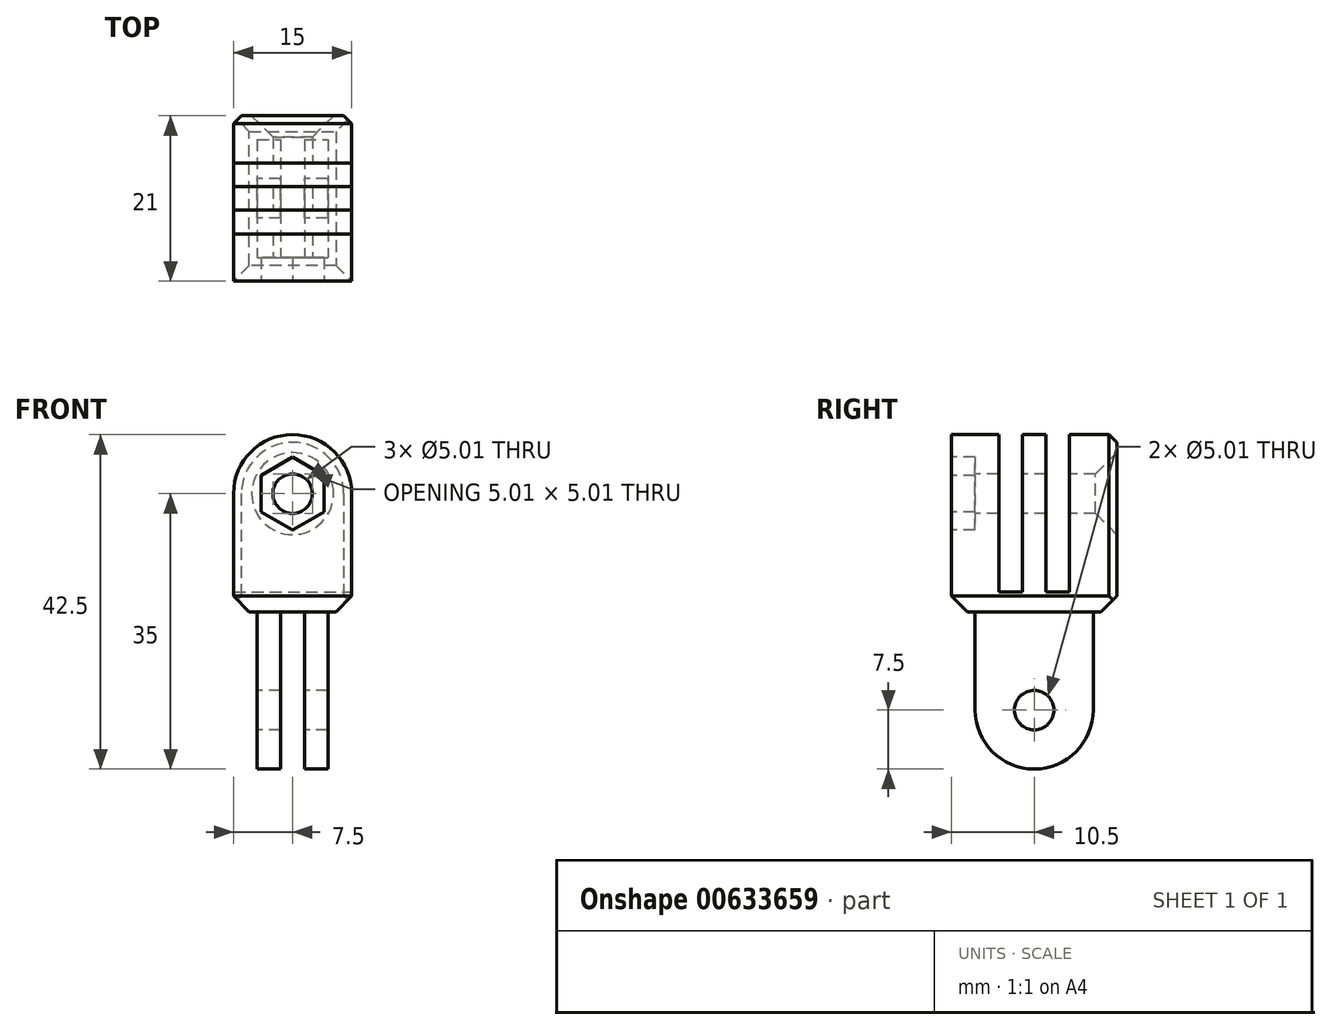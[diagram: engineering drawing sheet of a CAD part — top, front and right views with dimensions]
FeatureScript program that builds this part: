
annotation { "Feature Type Name" : "Feature", "Feature Type Description" : "" }
export const myFeature = defineFeature(function(context is Context, id is Id, definition is map)
    precondition{}
    {
        {
            var Q0;
            Q0=qCreatedBy(makeId("Top.planeOp"),FACE);
            var sketch = newSketch(context, id + "F0", { "sketchPlane" : qUnion([Q0])});
            skLineSegment(sketch, "E0.bottom", {"start": v(7.5, 10.5) * mm, "end": v(-7.5, 10.5) * mm});
            skLineSegment(sketch, "E0.top", {"start": v(7.5, -10.5) * mm, "end": v(-7.5, -10.5) * mm});
            skLineSegment(sketch, "E0.left", {"start": v(7.5, 10.5) * mm, "end": v(7.5, -10.5) * mm});
            skLineSegment(sketch, "E0.right", {"start": v(-7.5, 10.5) * mm, "end": v(-7.5, -10.5) * mm});
            skPoint(sketch, "E0.middle", {"position": v(0, 0) * mm});
            skSolve(sketch);
        }
        {
            var Q0;
            Q0 = qSketchRegion(id + "F0", true);
            extrude(context, id + "F1", {"entities" : qUnion([Q0]), "depth" : 2.5 * mm, "offsetDistance" : 25 * mm, "symmetric" : true});
        }
        {
            var Q0;
            Q0=makeQuery(id+"F1.opExtrude","CAP_FACE",FACE,{"disambiguationData":[OSD([sQuery(id+"F0.wireOp",EDGE,"E0.bottom"),sQuery(id+"F0.wireOp",EDGE,"E0.top"),sQuery(id+"F0.wireOp",EDGE,"E0.left"),sQuery(id+"F0.wireOp",EDGE,"E0.right")])],"isStart":false});
            var sketch = newSketch(context, id + "F2", { "sketchPlane" : qUnion([Q0])});
            skLineSegment(sketch, "E1", {"start": v(-7.5, 10.5) * mm, "end": v(-7.5, 4.5) * mm, "construction": true});
            skLineSegment(sketch, "E2", {"start": v(-7.5, 4.5) * mm, "end": v(-7.5, 1.5) * mm, "construction": true});
            skLineSegment(sketch, "E3", {"start": v(-7.5, 1.5) * mm, "end": v(-7.5, -1.5) * mm, "construction": true});
            skLineSegment(sketch, "E4", {"start": v(-7.5, -1.5) * mm, "end": v(-7.5, -4.5) * mm, "construction": true});
            skLineSegment(sketch, "E5", {"start": v(-7.5, 4.5) * mm, "end": v(7.5, 4.5) * mm});
            skLineSegment(sketch, "E6", {"start": v(-7.5, 1.5) * mm, "end": v(7.5, 1.5) * mm});
            skLineSegment(sketch, "E7", {"start": v(-7.5, -1.5) * mm, "end": v(7.5, -1.5) * mm});
            skLineSegment(sketch, "E8", {"start": v(-7.5, -4.5) * mm, "end": v(7.5, -4.5) * mm});
            skSolve(sketch);
        }
        {
            var Q0;
            Q0 = qSketchRegion(id + "F2", true);
            var Q1;
            {var subQ0=sQuery(id+"F2.wireOp",EDGE,"E8");Q1=makeQuery(id+"F2.imprint","IMPRINT",FACE,{"disambiguationData":[TD([[makeQuery(id+"F2.imprint","IMPRINT",EDGE,{"derivedFrom":subQ0}),-1.0]])]});}
            var Q2;
            {var subQ0=sQuery(id+"F2.wireOp",EDGE,"E6");Q2=makeQuery(id+"F2.imprint","IMPRINT",FACE,{"disambiguationData":[TD([[makeQuery(id+"F2.imprint","IMPRINT",EDGE,{"derivedFrom":subQ0}),-1.0]])]});}
            var Q3;
            {var subQ0=sQuery(id+"F2.wireOp",EDGE,"E5");Q3=makeQuery(id+"F2.imprint","IMPRINT",FACE,{"disambiguationData":[TD([[makeQuery(id+"F2.imprint","IMPRINT",EDGE,{"derivedFrom":subQ0}),1.0]])]});}
            extrude(context, id + "F3", {"entities" : qUnion([Q0, Q1, Q2, Q3]), "operationType" : NewBodyOperationType.ADD, "depth" : 20 * mm, "offsetDistance" : 25 * mm});
        }
        {
            var Q0;
            Q0=makeQuery(id+"F1.opExtrude","CAP_FACE",FACE,{"disambiguationData":[OSD([sQuery(id+"F0.wireOp",EDGE,"E0.bottom"),sQuery(id+"F0.wireOp",EDGE,"E0.top"),sQuery(id+"F0.wireOp",EDGE,"E0.left"),sQuery(id+"F0.wireOp",EDGE,"E0.right")])],"isStart":true});
            var sketch = newSketch(context, id + "F4", { "sketchPlane" : qUnion([Q0])});
            skLineSegment(sketch, "E9", {"start": v(-7.5, -10.5) * mm, "end": v(-4.5, -10.5) * mm, "construction": true});
            skLineSegment(sketch, "E10", {"start": v(-4.5, -10.5) * mm, "end": v(-1.5, -10.5) * mm, "construction": true});
            skLineSegment(sketch, "E11", {"start": v(-1.5, -10.5) * mm, "end": v(1.5, -10.5) * mm, "construction": true});
            skLineSegment(sketch, "E12", {"start": v(1.5, -10.5) * mm, "end": v(4.5, -10.5) * mm, "construction": true});
            skLineSegment(sketch, "E13", {"start": v(-4.5, -10.5) * mm, "end": v(-4.5, -7.5) * mm, "construction": true});
            skLineSegment(sketch, "E14", {"start": v(-7.5, 10.5) * mm, "end": v(-4.5, 10.5) * mm, "construction": true});
            skLineSegment(sketch, "E15", {"start": v(-4.5, 10.5) * mm, "end": v(-1.5, 10.5) * mm, "construction": true});
            skLineSegment(sketch, "E16", {"start": v(-1.5, 10.5) * mm, "end": v(1.5, 10.5) * mm, "construction": true});
            skLineSegment(sketch, "E17", {"start": v(1.5, 10.5) * mm, "end": v(4.5, 10.5) * mm, "construction": true});
            skLineSegment(sketch, "E18", {"start": v(4.5, 10.5) * mm, "end": v(4.5, 7.5) * mm, "construction": true});
            skLineSegment(sketch, "E19", {"start": v(4.5, 7.5) * mm, "end": v(1.5, 7.5) * mm, "construction": true});
            skLineSegment(sketch, "E20", {"start": v(1.5, 7.5) * mm, "end": v(-1.5, 7.5) * mm, "construction": true});
            skLineSegment(sketch, "E21", {"start": v(1.5, -10.5) * mm, "end": v(1.5, -7.5) * mm, "construction": true});
            skLineSegment(sketch, "E22.bottom", {"start": v(-4.5, -7.5) * mm, "end": v(-1.5, -7.5) * mm});
            skLineSegment(sketch, "E22.top", {"start": v(-4.5, 7.5) * mm, "end": v(-1.5, 7.5) * mm});
            skLineSegment(sketch, "E22.left", {"start": v(-4.5, -7.5) * mm, "end": v(-4.5, 7.5) * mm});
            skLineSegment(sketch, "E22.right", {"start": v(-1.5, -7.5) * mm, "end": v(-1.5, 7.5) * mm});
            skLineSegment(sketch, "E23.bottom", {"start": v(1.5, -7.5) * mm, "end": v(4.5, -7.5) * mm});
            skLineSegment(sketch, "E23.top", {"start": v(1.5, 7.5) * mm, "end": v(4.5, 7.5) * mm});
            skLineSegment(sketch, "E23.left", {"start": v(1.5, -7.5) * mm, "end": v(1.5, 7.5) * mm});
            skLineSegment(sketch, "E23.right", {"start": v(4.5, -7.5) * mm, "end": v(4.5, 7.5) * mm});
            skSolve(sketch);
        }
        {
            var Q0;
            Q0=makeQuery(id+"F4.imprint","IMPRINT",FACE,{"disambiguationData":[TD([[makeQuery(id+"F4.imprint","IMPRINT",EDGE,{"derivedFrom":sQuery(id+"F4.wireOp",EDGE,"E22.bottom")}),1.0]])]});
            var Q1;
            Q1=makeQuery(id+"F4.imprint","IMPRINT",FACE,{"disambiguationData":[TD([[makeQuery(id+"F4.imprint","IMPRINT",EDGE,{"derivedFrom":sQuery(id+"F4.wireOp",EDGE,"E23.bottom")}),1.0]])]});
            extrude(context, id + "F5", {"entities" : qUnion([Q0, Q1]), "operationType" : NewBodyOperationType.ADD, "depth" : 20 * mm, "offsetDistance" : 25 * mm});
        }
        {
            var Q0;
            {var subQ0=sQuery(id+"F0.wireOp",EDGE,"E0.top");Q0=makeQuery(id+"F3.boolean.opBoolean","MERGE",FACE,{"derivedFrom":[makeQuery(id+"F1.opExtrude","SWEPT_FACE",FACE,{"disambiguationData":[OSD([subQ0])]}),makeQuery(id+"F3.opExtrude","SWEPT_FACE",FACE,{"disambiguationData":[OSD([subQ0])]})]});}
            var sketch = newSketch(context, id + "F6", { "sketchPlane" : qUnion([Q0])});
            skLineSegment(sketch, "E24", {"start": v(0, 21.25) * mm, "end": v(0, 13.75) * mm, "construction": true});
            skPoint(sketch, "E24.endSnap0", {"position": v(0, 21.25) * mm});
            skCircle(sketch, "E25", {"center": v(0, 13.75) * mm, "radius": 7.5 * mm});
            skCircle(sketch, "E26", {"center": v(0, 13.75) * mm, "radius": 2.5 * mm});
            skCircle(sketch, "E27.cCircle", {"center": v(0, 13.75) * mm, "radius": 4.01 * mm, "construction": true});
            skLineSegment(sketch, "E27.0", {"start": v(0, 18.38) * mm, "end": v(4, 16.07) * mm});
            skLineSegment(sketch, "E27.1", {"start": v(4, 16.07) * mm, "end": v(4.01, 11.44) * mm});
            skLineSegment(sketch, "E27.2", {"start": v(4.01, 11.44) * mm, "end": v(0, 9.12) * mm});
            skLineSegment(sketch, "E27.3", {"start": v(0, 9.12) * mm, "end": v(-4, 11.43) * mm});
            skLineSegment(sketch, "E27.4", {"start": v(-4, 11.43) * mm, "end": v(-4.01, 16.06) * mm});
            skLineSegment(sketch, "E27.5", {"start": v(-4.01, 16.06) * mm, "end": v(0, 18.38) * mm});
            skPoint(sketch, "E27.0.midPoint", {"position": v(2, 17.22) * mm});
            skLineSegment(sketch, "E28", {"start": v(0, 13.75) * mm, "end": v(2, 17.22) * mm, "construction": true});
            skSolve(sketch);
        }
        {
            var Q0;
            {var subQ0=sQuery(id+"F6.wireOp",EDGE,"E25");var subQ1=sQuery(id+"F0.wireOp",EDGE,"E0.top");var subQ2=makeQuery(id+"F3.opExtrude","CAP_EDGE",EDGE,{"disambiguationData":[OSD([subQ1])],"isStart":false});var subQ3=makeQuery(id+"F6.imprint","INTERSECT",VERTEX,{"derivedFrom":[subQ2,subQ0]});Q0=makeQuery(id+"F6.imprint","IMPRINT",FACE,{"disambiguationData":[TD([[makeQuery(id+"F6.imprint","IMPRINT",EDGE,{"disambiguationData":[TD([[subQ3,1.0]])],"derivedFrom":subQ0}),-1.0]])]});}
            var Q1;
            {var subQ0=sQuery(id+"F6.wireOp",EDGE,"E25");var subQ1=sQuery(id+"F0.wireOp",EDGE,"E0.top");var subQ2=makeQuery(id+"F3.opExtrude","CAP_EDGE",EDGE,{"disambiguationData":[OSD([subQ1])],"isStart":false});var subQ3=makeQuery(id+"F6.imprint","INTERSECT",VERTEX,{"derivedFrom":[subQ2,subQ0]});Q1=makeQuery(id+"F6.imprint","IMPRINT",FACE,{"disambiguationData":[TD([[makeQuery(id+"F6.imprint","IMPRINT",EDGE,{"disambiguationData":[TD([[subQ3,-1.0]])],"derivedFrom":subQ0}),-1.0]])]});}
            var Q2;
            Q2=makeQuery(id+"F6.imprint","IMPRINT",FACE,{"disambiguationData":[TD([[makeQuery(id+"F6.imprint","IMPRINT",EDGE,{"derivedFrom":sQuery(id+"F6.wireOp",EDGE,"E26")}),1.0]])]});
            extrude(context, id + "F7", {"entities" : qUnion([Q0, Q1, Q2]), "operationType" : NewBodyOperationType.REMOVE, "oppositeDirection" : true, "depth" : 25 * mm, "offsetDistance" : 25 * mm});
        }
        {
            var Q0;
            Q0=makeQuery(id+"F5.opExtrude","SWEPT_FACE",FACE,{"disambiguationData":[OSD([sQuery(id+"F4.wireOp",EDGE,"E22.left")])]});
            var sketch = newSketch(context, id + "F8", { "sketchPlane" : qUnion([Q0])});
            skLineSegment(sketch, "E29", {"start": v(0, -21.25) * mm, "end": v(0, -13.75) * mm, "construction": true});
            skPoint(sketch, "E29.endSnap0", {"position": v(0, -21.25) * mm});
            skCircle(sketch, "E30", {"center": v(0, -13.75) * mm, "radius": 7.5 * mm});
            skCircle(sketch, "E31", {"center": v(0, -13.75) * mm, "radius": 2.5 * mm});
            skSolve(sketch);
        }
        {
            var Q0;
            {var subQ0=sQuery(id+"F8.wireOp",EDGE,"E30");var subQ1=sQuery(id+"F4.wireOp",EDGE,"E22.left");var subQ4=makeQuery(id+"F5.opExtrude","CAP_EDGE",EDGE,{"disambiguationData":[OSD([subQ1])],"isStart":false});var subQ5=makeQuery(id+"F8.imprint","INTERSECT",VERTEX,{"derivedFrom":[subQ4,subQ0]});Q0=makeQuery(id+"F8.imprint","IMPRINT",FACE,{"disambiguationData":[TD([[makeQuery(id+"F8.imprint","IMPRINT",EDGE,{"disambiguationData":[TD([[subQ5,-1.0]])],"derivedFrom":subQ0}),-1.0]])]});}
            var Q1;
            {var subQ0=sQuery(id+"F8.wireOp",EDGE,"E30");var subQ1=sQuery(id+"F4.wireOp",EDGE,"E22.left");var subQ4=makeQuery(id+"F5.opExtrude","CAP_EDGE",EDGE,{"disambiguationData":[OSD([subQ1])],"isStart":false});var subQ5=makeQuery(id+"F8.imprint","INTERSECT",VERTEX,{"derivedFrom":[subQ4,subQ0]});Q1=makeQuery(id+"F8.imprint","IMPRINT",FACE,{"disambiguationData":[TD([[makeQuery(id+"F8.imprint","IMPRINT",EDGE,{"disambiguationData":[TD([[subQ5,1.0]])],"derivedFrom":subQ0}),-1.0]])]});}
            var Q2;
            Q2=makeQuery(id+"F8.imprint","IMPRINT",FACE,{"disambiguationData":[TD([[makeQuery(id+"F8.imprint","IMPRINT",EDGE,{"derivedFrom":sQuery(id+"F8.wireOp",EDGE,"E31")}),1.0]])]});
            extrude(context, id + "F9", {"entities" : qUnion([Q0, Q1, Q2]), "operationType" : NewBodyOperationType.REMOVE, "oppositeDirection" : true, "depth" : 25 * mm, "offsetDistance" : 25 * mm});
        }
        {
            var Q0;
            Q0=makeQuery(id+"F1.opExtrude","CAP_EDGE",EDGE,{"disambiguationData":[OSD([sQuery(id+"F0.wireOp",EDGE,"E0.right")])],"isStart":true});
            var Q1;
            Q1=makeQuery(id+"F1.opExtrude","CAP_EDGE",EDGE,{"disambiguationData":[OSD([sQuery(id+"F0.wireOp",EDGE,"E0.bottom")])],"isStart":true});
            var Q2;
            Q2=makeQuery(id+"F1.opExtrude","CAP_EDGE",EDGE,{"disambiguationData":[OSD([sQuery(id+"F0.wireOp",EDGE,"E0.top")])],"isStart":true});
            var Q3;
            Q3=makeQuery(id+"F1.opExtrude","CAP_EDGE",EDGE,{"disambiguationData":[OSD([sQuery(id+"F0.wireOp",EDGE,"E0.left")])],"isStart":true});
            chamfer(context, id + "F10", {"entities" : qUnion([Q0, Q1, Q2, Q3]), "width" : 2 * mm, "tangentPropagation" : true});
        }
        {
            var Q0;
            Q0=makeQuery(id+"F6.imprint","IMPRINT",FACE,{"disambiguationData":[TD([[makeQuery(id+"F6.imprint","IMPRINT",EDGE,{"derivedFrom":sQuery(id+"F6.wireOp",EDGE,"E26")}),-1.0]])]});
            extrude(context, id + "F11", {"entities" : qUnion([Q0]), "operationType" : NewBodyOperationType.REMOVE, "oppositeDirection" : true, "depth" : 3 * mm, "offsetDistance" : 25 * mm});
        }
        {
            var Q0;
            {var subQ0=sQuery(id+"F0.wireOp",EDGE,"E0.bottom");Q0=makeQuery(id+"F7.boolean.opBoolean","INTERSECT",EDGE,{"derivedFrom":[makeQuery(id+"F3.boolean.opBoolean","MERGE",FACE,{"derivedFrom":[makeQuery(id+"F1.opExtrude","SWEPT_FACE",FACE,{"disambiguationData":[OSD([subQ0])]}),makeQuery(id+"F3.opExtrude","SWEPT_FACE",FACE,{"disambiguationData":[OSD([subQ0])]})]}),makeQuery(id+"F7.opExtrude","SWEPT_FACE",FACE,{"disambiguationData":[OSD([sQuery(id+"F6.wireOp",EDGE,"E26")])]})]});}
            chamfer(context, id + "F12", {"entities" : qUnion([Q0]), "width" : 2.7 * mm, "tangentPropagation" : true});
        }
        {
            var Q0;
            {var subQ0=sQuery(id+"F6.wireOp",EDGE,"E25");var subQ1=sQuery(id+"F0.wireOp",EDGE,"E0.top");var subQ2=makeQuery(id+"F6.imprint","INTERSECT",VERTEX,{"derivedFrom":[makeQuery(id+"F3.opExtrude","CAP_EDGE",EDGE,{"disambiguationData":[OSD([subQ1])],"isStart":false}),subQ0]});Q0=makeQuery(id+"F7.boolean.opBoolean","TWEAK_EDGE",EDGE,{"derivedFrom":[makeQuery(id+"F7.opExtrude","CAP_EDGE",EDGE,{"disambiguationData":[OSD([subQ0]),TDD([makeQuery(id+"F6.imprint","IMPRINT",EDGE,{"disambiguationData":[TD([[subQ2,1.0]])],"derivedFrom":subQ0})])],"isStart":true}),makeQuery(id+"F7.opExtrude","CAP_EDGE",EDGE,{"disambiguationData":[OSD([subQ0]),TDD([makeQuery(id+"F6.imprint","IMPRINT",EDGE,{"disambiguationData":[TD([[subQ2,-1.0]])],"derivedFrom":subQ0})])],"isStart":true})]});}
            var Q1;
            {var subQ0=sQuery(id+"F6.wireOp",EDGE,"E25");var subQ1=sQuery(id+"F0.wireOp",EDGE,"E0.top");var subQ2=makeQuery(id+"F6.imprint","INTERSECT",VERTEX,{"derivedFrom":[makeQuery(id+"F3.opExtrude","CAP_EDGE",EDGE,{"disambiguationData":[OSD([subQ1])],"isStart":false}),subQ0]});var subQ5=sQuery(id+"F0.wireOp",EDGE,"E0.bottom");Q1=makeQuery(id+"F7.boolean.opBoolean","INTERSECT",EDGE,{"derivedFrom":[makeQuery(id+"F3.boolean.opBoolean","MERGE",FACE,{"derivedFrom":[makeQuery(id+"F1.opExtrude","SWEPT_FACE",FACE,{"disambiguationData":[OSD([subQ5])]}),makeQuery(id+"F3.opExtrude","SWEPT_FACE",FACE,{"disambiguationData":[OSD([subQ5])]})]}),makeQuery(id+"F7.opExtrude","SWEPT_FACE",FACE,{"disambiguationData":[OSD([subQ0]),TDD([makeQuery(id+"F6.imprint","IMPRINT",EDGE,{"disambiguationData":[TD([[subQ2,1.0]])],"derivedFrom":subQ0})])]}),makeQuery(id+"F7.opExtrude","SWEPT_FACE",FACE,{"disambiguationData":[OSD([subQ0]),TDD([makeQuery(id+"F6.imprint","IMPRINT",EDGE,{"disambiguationData":[TD([[subQ2,-1.0]])],"derivedFrom":subQ0})])]})]});}
            chamfer(context, id + "F13", {"entities" : qUnion([Q0, Q1]), "width" : 1 * mm, "tangentPropagation" : true});
        }
    });
